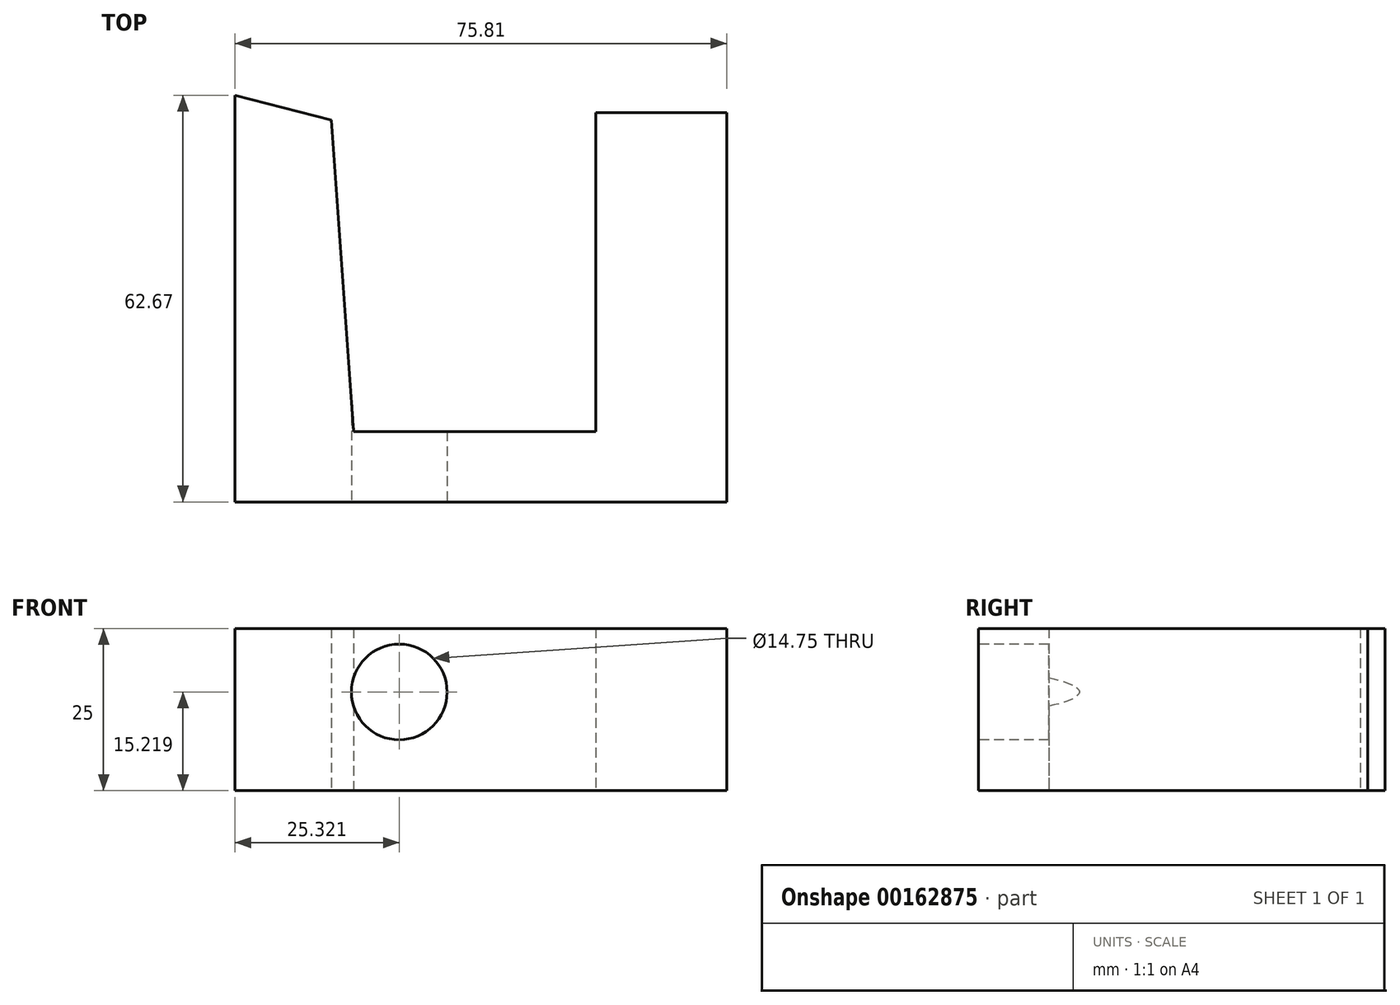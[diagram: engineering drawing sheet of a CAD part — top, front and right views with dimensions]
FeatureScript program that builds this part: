
annotation { "Feature Type Name" : "Feature", "Feature Type Description" : "" }
export const myFeature = defineFeature(function(context is Context, id is Id, definition is map)
    precondition{}
    {
        {
            var Q0;
            Q0=qCreatedBy(makeId("Top.planeOp"),FACE);
            var sketch = newSketch(context, id + "F0", { "sketchPlane" : qUnion([Q0])});
            skLineSegment(sketch, "E0", {"start": v(0, 0) * mm, "end": v(75.8, 0) * mm});
            skLineSegment(sketch, "E1", {"start": v(75.8, 0) * mm, "end": v(75.8, 60) * mm});
            skLineSegment(sketch, "E2", {"start": v(75.8, 60) * mm, "end": v(55.62, 60) * mm});
            skLineSegment(sketch, "E3", {"start": v(55.62, 60) * mm, "end": v(55.62, 10.86) * mm});
            skLineSegment(sketch, "E4", {"start": v(55.62, 10.86) * mm, "end": v(18.29, 10.86) * mm});
            skLineSegment(sketch, "E5", {"start": v(18.29, 10.86) * mm, "end": v(14.86, 58.86) * mm});
            skLineSegment(sketch, "E6", {"start": v(14.86, 58.86) * mm, "end": v(0, 62.67) * mm});
            skLineSegment(sketch, "E7", {"start": v(0, 62.67) * mm, "end": v(0, 0) * mm});
            skSolve(sketch);
        }
        {
            var Q0;
            Q0 = qSketchRegion(id + "F0", true);
            extrude(context, id + "F1", {"entities" : qUnion([Q0]), "depth" : 25 * mm});
        }
        {
            var Q0;
            Q0=makeQuery(id+"F1.opExtrude","SWEPT_FACE",FACE,{"disambiguationData":[OSD([sQuery(id+"F0.wireOp",EDGE,"E0")])]});
            var sketch = newSketch(context, id + "F2", { "sketchPlane" : qUnion([Q0])});
            skCircle(sketch, "E8", {"center": v(25.32, 15.22) * mm, "radius": 7.37 * mm});
            skSolve(sketch);
        }
        {
            var Q0;
            Q0 = qSketchRegion(id + "F2", true);
            extrude(context, id + "F3", {"entities" : qUnion([Q0]), "operationType" : NewBodyOperationType.REMOVE, "oppositeDirection" : true, "depth" : 25 * mm});
        }
    });
